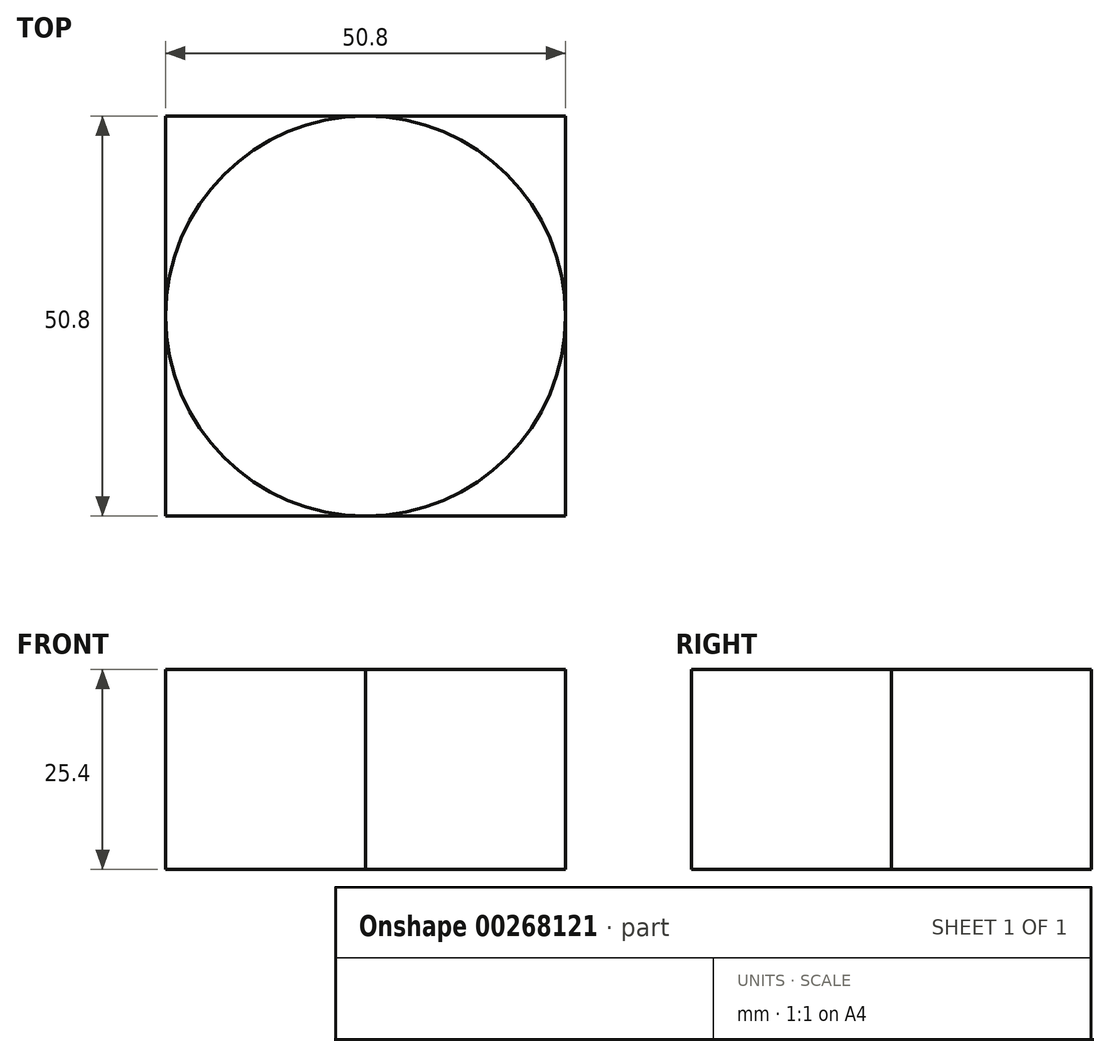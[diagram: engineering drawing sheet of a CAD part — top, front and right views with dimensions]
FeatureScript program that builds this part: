
annotation { "Feature Type Name" : "Feature", "Feature Type Description" : "" }
export const myFeature = defineFeature(function(context is Context, id is Id, definition is map)
    precondition{}
    {
        {
            var Q0;
            Q0=qCreatedBy(makeId("Top.planeOp"),FACE);
            var sketch = newSketch(context, id + "F0", { "sketchPlane" : qUnion([Q0])});
            skCircle(sketch, "E0", {"center": v(0, 0) * mm, "radius": 25.4 * mm});
            skLineSegment(sketch, "E1", {"start": v(-25.4, -25.4) * mm, "end": v(-25.4, 25.4) * mm});
            skLineSegment(sketch, "E2", {"start": v(-25.4, -25.4) * mm, "end": v(25.4, -25.4) * mm});
            skLineSegment(sketch, "E3", {"start": v(-25.4, 25.4) * mm, "end": v(25.4, 25.4) * mm});
            skLineSegment(sketch, "E4", {"start": v(25.4, 25.4) * mm, "end": v(25.4, -25.4) * mm});
            skSolve(sketch);
        }
        {
            var Q0;
            {var subQ0=sQuery(id+"F0.wireOp",EDGE,"E3");var subQ1=sQuery(id+"F0.wireOp",EDGE,"E0");var subQ2=makeQuery(id+"F0.imprint","INTERSECT",VERTEX,{"derivedFrom":[subQ1,subQ0]});Q0=makeQuery(id+"F0.imprint","IMPRINT",FACE,{"disambiguationData":[TD([[makeQuery(id+"F0.imprint","IMPRINT",EDGE,{"disambiguationData":[TD([[subQ2,1.0]])],"derivedFrom":subQ1}),-1.0]])]});}
            var Q1;
            {var subQ0=sQuery(id+"F0.wireOp",EDGE,"E3");var subQ1=sQuery(id+"F0.wireOp",EDGE,"E0");var subQ2=makeQuery(id+"F0.imprint","INTERSECT",VERTEX,{"derivedFrom":[subQ1,subQ0]});Q1=makeQuery(id+"F0.imprint","IMPRINT",FACE,{"disambiguationData":[TD([[makeQuery(id+"F0.imprint","IMPRINT",EDGE,{"disambiguationData":[TD([[subQ2,-1.0]])],"derivedFrom":subQ1}),-1.0]])]});}
            var Q2;
            {var subQ0=sQuery(id+"F0.wireOp",EDGE,"E1");var subQ1=sQuery(id+"F0.wireOp",EDGE,"E0");var subQ2=makeQuery(id+"F0.imprint","INTERSECT",VERTEX,{"derivedFrom":[subQ1,subQ0]});Q2=makeQuery(id+"F0.imprint","IMPRINT",FACE,{"disambiguationData":[TD([[makeQuery(id+"F0.imprint","IMPRINT",EDGE,{"disambiguationData":[TD([[subQ2,-1.0]])],"derivedFrom":subQ1}),-1.0]])]});}
            var Q3;
            {var subQ0=sQuery(id+"F0.wireOp",EDGE,"E4");var subQ1=sQuery(id+"F0.wireOp",EDGE,"E0");var subQ2=makeQuery(id+"F0.imprint","INTERSECT",VERTEX,{"derivedFrom":[subQ1,subQ0]});Q3=makeQuery(id+"F0.imprint","IMPRINT",FACE,{"disambiguationData":[TD([[makeQuery(id+"F0.imprint","IMPRINT",EDGE,{"disambiguationData":[TD([[subQ2,1.0]])],"derivedFrom":subQ1}),-1.0]])]});}
            extrude(context, id + "F1", {"entities" : qUnion([Q0, Q1, Q2, Q3]), "depth" : 25.4 * mm});
        }
    });
